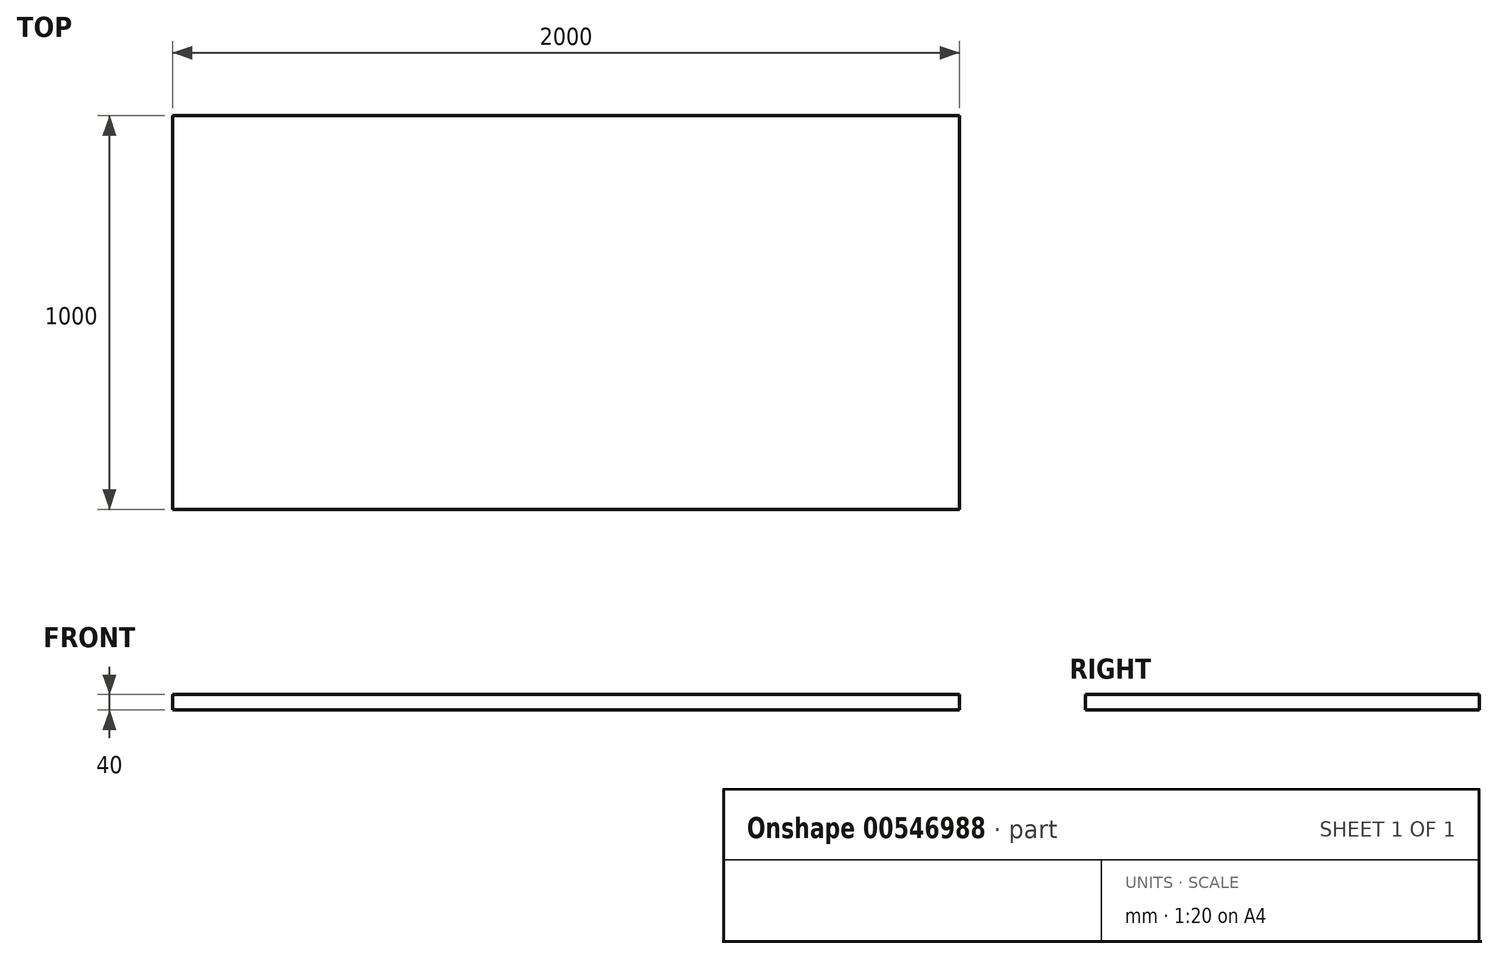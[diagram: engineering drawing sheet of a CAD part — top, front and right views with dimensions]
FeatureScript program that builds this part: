
annotation { "Feature Type Name" : "Feature", "Feature Type Description" : "" }
export const myFeature = defineFeature(function(context is Context, id is Id, definition is map)
    precondition{}
    {
        {
            var Q0;
            Q0=qCreatedBy(makeId("Top.planeOp"),FACE);
            var sketch = newSketch(context, id + "F0", { "sketchPlane" : qUnion([Q0])});
            skLineSegment(sketch, "E0.bottom", {"start": v(-990.27, -524.7) * mm, "end": v(1009.73, -524.7) * mm});
            skLineSegment(sketch, "E0.top", {"start": v(-990.27, 475.3) * mm, "end": v(1009.73, 475.3) * mm});
            skLineSegment(sketch, "E0.left", {"start": v(-990.27, -524.7) * mm, "end": v(-990.27, 475.3) * mm});
            skLineSegment(sketch, "E0.right", {"start": v(1009.73, -524.7) * mm, "end": v(1009.73, 475.3) * mm});
            skSolve(sketch);
        }
        {
            var Q0;
            Q0=makeQuery(id+"F0.imprint","IMPRINT",FACE,{"disambiguationData":[TD([[makeQuery(id+"F0.imprint","IMPRINT",EDGE,{"derivedFrom":sQuery(id+"F0.wireOp",EDGE,"E0.bottom")}),1.0]])]});
            extrude(context, id + "F1", {"entities" : qUnion([Q0]), "depth" : 40 * mm, "offsetDistance" : 25 * mm});
        }
    });
